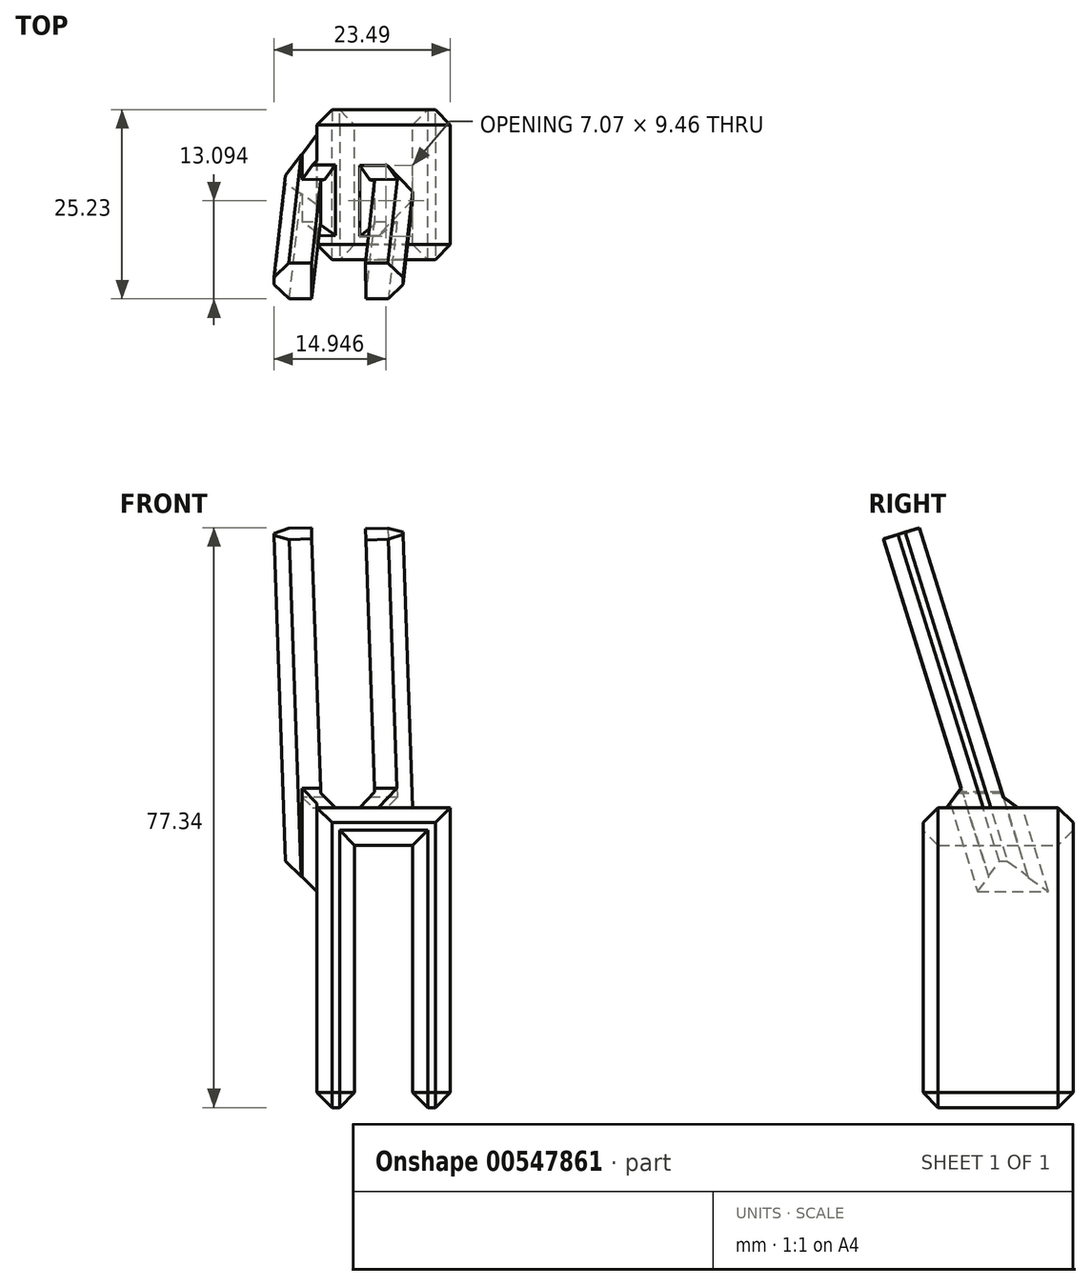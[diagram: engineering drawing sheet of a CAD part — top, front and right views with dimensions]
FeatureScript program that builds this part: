
annotation { "Feature Type Name" : "Feature", "Feature Type Description" : "" }
export const myFeature = defineFeature(function(context is Context, id is Id, definition is map)
    precondition{}
    {
        {
            var Q0;
            Q0=qCreatedBy(makeId("Front.planeOp"),FACE);
            var sketch = newSketch(context, id + "F0", { "sketchPlane" : qUnion([Q0])});
            skLineSegment(sketch, "E0", {"start": v(0, 17.78) * mm, "end": v(40, 17.78) * mm});
            skLineSegment(sketch, "E1", {"start": v(40, 17.78) * mm, "end": v(40, 0.03) * mm});
            skLineSegment(sketch, "E2", {"start": v(40, 0.03) * mm, "end": v(0, 0.03) * mm});
            skLineSegment(sketch, "E3", {"start": v(0, 0.03) * mm, "end": v(0, 5.03) * mm});
            skLineSegment(sketch, "E4", {"start": v(0, 5.03) * mm, "end": v(35, 5.03) * mm});
            skLineSegment(sketch, "E5", {"start": v(35, 5.03) * mm, "end": v(35, 12.78) * mm});
            skLineSegment(sketch, "E6", {"start": v(35, 12.78) * mm, "end": v(0, 12.78) * mm});
            skLineSegment(sketch, "E7", {"start": v(0, 12.78) * mm, "end": v(0, 17.78) * mm});
            skSolve(sketch);
        }
        {
            var Q0;
            Q0=makeQuery(id+"F0.imprint","IMPRINT",FACE,{"disambiguationData":[TD([[makeQuery(id+"F0.imprint","IMPRINT",EDGE,{"derivedFrom":sQuery(id+"F0.wireOp",EDGE,"E0")}),-1.0]])]});
            extrude(context, id + "F1", {"entities" : qUnion([Q0]), "endBound" : BoundingType.SYMMETRIC, "depth" : 20 * mm, "offsetDistance" : 25 * mm});
        }
        {
            var Q0;
            Q0=qCreatedBy(makeId("Top.planeOp"),FACE);
            var sketch = newSketch(context, id + "F2", { "sketchPlane" : qUnion([Q0])});
            skLineSegment(sketch, "E8", {"start": v(39, 1.42) * mm, "end": v(77.2, -10.46) * mm});
            skLineSegment(sketch, "E9", {"start": v(77.2, -10.46) * mm, "end": v(75.71, -15.23) * mm});
            skLineSegment(sketch, "E10", {"start": v(75.71, -15.23) * mm, "end": v(39, -3.82) * mm});
            skLineSegment(sketch, "E11", {"start": v(39, -3.82) * mm, "end": v(39, 1.42) * mm});
            skSolve(sketch);
        }
        {
            var Q0;
            Q0=makeQuery(id+"F2.imprint","IMPRINT",FACE,{"disambiguationData":[TD([[makeQuery(id+"F2.imprint","IMPRINT",EDGE,{"derivedFrom":sQuery(id+"F2.wireOp",EDGE,"E8")}),-1.0]])]});
            var Q1;
            Q1=sQuery(id+"F2.wireOp",EDGE,"E10");
            var Q2;
            Q2=sQuery(id+"F2.wireOp",EDGE,"E9");
            var Q3;
            Q3=sQuery(id+"F2.wireOp",EDGE,"E11");
            var Q4;
            Q4=sQuery(id+"F2.wireOp",EDGE,"E8");
            extrude(context, id + "F3", {"entities" : qUnion([Q0]), "surfaceEntities" : qUnion([Q1, Q2, Q3, Q4]), "depth" : 5 * mm, "offsetDistance" : 25 * mm});
        }
        {
            var Q0;
            Q0=makeQuery(id+"F3.opExtrude","SWEPT_BODY",BODY,{"disambiguationData":[OSD([sQuery(id+"F2.wireOp",EDGE,"E8"),sQuery(id+"F2.wireOp",EDGE,"E9"),sQuery(id+"F2.wireOp",EDGE,"E10"),sQuery(id+"F2.wireOp",EDGE,"E11")])]});
            var Q1;
            Q1=makeQuery(id+"F3.opExtrude","CAP_EDGE",EDGE,{"disambiguationData":[OSD([sQuery(id+"F2.wireOp",EDGE,"E11")])],"isStart":false});
            transform(context, id + "F4", {"entities" : qUnion([Q0]), "transformType" : TransformType.ROTATION, "transformAxis" : qUnion([Q1]), "angle" : 2 * degree, "oppositeDirection" : true, "makeCopy" : false});
        }
        {
            var Q0;
            Q0=makeQuery(id+"F3.opExtrude","SWEPT_BODY",BODY,{"disambiguationData":[OSD([sQuery(id+"F2.wireOp",EDGE,"E8"),sQuery(id+"F2.wireOp",EDGE,"E9"),sQuery(id+"F2.wireOp",EDGE,"E10"),sQuery(id+"F2.wireOp",EDGE,"E11")])]});
            var Q1;
            Q1=qCreatedBy(makeId("Top.planeOp"),FACE);
            transform(context, id + "F5", {"entities" : qUnion([Q0]), "transformType" : TransformType.TRANSLATION_DISTANCE, "transformDirection" : qUnion([Q1]), "distance" : 5 * mm, "makeCopy" : false});
        }
        {
            var Q0;
            Q0=makeQuery(id+"F3.opExtrude","SWEPT_BODY",BODY,{"disambiguationData":[OSD([sQuery(id+"F2.wireOp",EDGE,"E8"),sQuery(id+"F2.wireOp",EDGE,"E9"),sQuery(id+"F2.wireOp",EDGE,"E10"),sQuery(id+"F2.wireOp",EDGE,"E11")])]});
            transform(context, id + "F6", {"entities" : qUnion([Q0]), "transformType" : TransformType.COPY});
        }
        {
            var Q0;
            Q0=makeQuery(id+"F3.opExtrude","SWEPT_BODY",BODY,{"disambiguationData":[OSD([sQuery(id+"F2.wireOp",EDGE,"E8"),sQuery(id+"F2.wireOp",EDGE,"E9"),sQuery(id+"F2.wireOp",EDGE,"E10"),sQuery(id+"F2.wireOp",EDGE,"E11")])]});
            var Q1;
            Q1=qCreatedBy(makeId("Top.planeOp"),FACE);
            transform(context, id + "F7", {"entities" : qUnion([Q0]), "transformType" : TransformType.TRANSLATION_DISTANCE, "transformDirection" : qUnion([Q1]), "distance" : 12.2 * mm, "makeCopy" : false});
        }
        {
            var Q0;
            Q0=makeQuery(id+"F1.opExtrude","SWEPT_BODY",BODY,{"disambiguationData":[OSD([sQuery(id+"F0.wireOp",EDGE,"E0"),sQuery(id+"F0.wireOp",EDGE,"E1"),sQuery(id+"F0.wireOp",EDGE,"E2"),sQuery(id+"F0.wireOp",EDGE,"E3"),sQuery(id+"F0.wireOp",EDGE,"E4"),sQuery(id+"F0.wireOp",EDGE,"E5"),sQuery(id+"F0.wireOp",EDGE,"E6"),sQuery(id+"F0.wireOp",EDGE,"E7")])]});
            var Q1;
            Q1=makeQuery(id+"F3.opExtrude","SWEPT_BODY",BODY,{"disambiguationData":[OSD([sQuery(id+"F2.wireOp",EDGE,"E8"),sQuery(id+"F2.wireOp",EDGE,"E9"),sQuery(id+"F2.wireOp",EDGE,"E10"),sQuery(id+"F2.wireOp",EDGE,"E11")])]});
            var Q2;
            Q2=makeQuery(id+"F6.opPattern","COPY",BODY,{"derivedFrom":makeQuery(id+"F3.opExtrude","SWEPT_BODY",BODY,{"disambiguationData":[OSD([sQuery(id+"F2.wireOp",EDGE,"E8"),sQuery(id+"F2.wireOp",EDGE,"E9"),sQuery(id+"F2.wireOp",EDGE,"E10"),sQuery(id+"F2.wireOp",EDGE,"E11")])]}),"instanceName":"1"});
            booleanBodies(context, id + "F8", {"operationType" : BooleanOperationType.UNION, "tools" : qUnion([Q0, Q1, Q2])});
        }
        {
            var Q0;
            Q0=makeQuery(id+"F8.opBoolean","INTERSECT",EDGE,{"derivedFrom":[makeQuery(id+"F1.opExtrude","SWEPT_FACE",FACE,{"disambiguationData":[OSD([sQuery(id+"F0.wireOp",EDGE,"E0")])]}),makeQuery(id+"F3.opExtrude","SWEPT_FACE",FACE,{"disambiguationData":[OSD([sQuery(id+"F2.wireOp",EDGE,"E11")])]})]});
            chamfer(context, id + "F9", {"entities" : qUnion([Q0]), "width" : 10 * mm, "tangentPropagation" : true});
        }
        {
            var Q0;
            Q0=makeQuery(id+"F3.opExtrude","CAP_EDGE",EDGE,{"disambiguationData":[OSD([sQuery(id+"F2.wireOp",EDGE,"E10")])],"isStart":false});
            var Q1;
            Q1=makeQuery(id+"F3.opExtrude","CAP_EDGE",EDGE,{"disambiguationData":[OSD([sQuery(id+"F2.wireOp",EDGE,"E8")])],"isStart":false});
            var Q2;
            Q2=makeQuery(id+"F6.opPattern","COPY",EDGE,{"derivedFrom":makeQuery(id+"F3.opExtrude","CAP_EDGE",EDGE,{"disambiguationData":[OSD([sQuery(id+"F2.wireOp",EDGE,"E10")])],"isStart":true}),"instanceName":"1"});
            var Q3;
            Q3=makeQuery(id+"F6.opPattern","COPY",EDGE,{"derivedFrom":makeQuery(id+"F3.opExtrude","CAP_EDGE",EDGE,{"disambiguationData":[OSD([sQuery(id+"F2.wireOp",EDGE,"E8")])],"isStart":true}),"instanceName":"1"});
            var Q4;
            Q4=makeQuery(id+"F1.opExtrude","CAP_FACE",FACE,{"disambiguationData":[OSD([sQuery(id+"F0.wireOp",EDGE,"E0"),sQuery(id+"F0.wireOp",EDGE,"E1"),sQuery(id+"F0.wireOp",EDGE,"E2"),sQuery(id+"F0.wireOp",EDGE,"E3"),sQuery(id+"F0.wireOp",EDGE,"E4"),sQuery(id+"F0.wireOp",EDGE,"E5"),sQuery(id+"F0.wireOp",EDGE,"E6"),sQuery(id+"F0.wireOp",EDGE,"E7")])],"isStart":false});
            var Q5;
            Q5=makeQuery(id+"F1.opExtrude","CAP_FACE",FACE,{"disambiguationData":[OSD([sQuery(id+"F0.wireOp",EDGE,"E0"),sQuery(id+"F0.wireOp",EDGE,"E1"),sQuery(id+"F0.wireOp",EDGE,"E2"),sQuery(id+"F0.wireOp",EDGE,"E3"),sQuery(id+"F0.wireOp",EDGE,"E4"),sQuery(id+"F0.wireOp",EDGE,"E5"),sQuery(id+"F0.wireOp",EDGE,"E6"),sQuery(id+"F0.wireOp",EDGE,"E7")])],"isStart":true});
            var Q6;
            Q6=makeQuery(id+"F1.opExtrude","SWEPT_EDGE",EDGE,{"disambiguationData":[OSD([sQuery(id+"F0.wireOp",EDGE,"E0"),sQuery(id+"F0.wireOp",EDGE,"E7")])]});
            var Q7;
            Q7=makeQuery(id+"F1.opExtrude","SWEPT_EDGE",EDGE,{"disambiguationData":[OSD([sQuery(id+"F0.wireOp",EDGE,"E6"),sQuery(id+"F0.wireOp",EDGE,"E7")])]});
            var Q8;
            Q8=makeQuery(id+"F1.opExtrude","SWEPT_EDGE",EDGE,{"disambiguationData":[OSD([sQuery(id+"F0.wireOp",EDGE,"E3"),sQuery(id+"F0.wireOp",EDGE,"E4")])]});
            var Q9;
            Q9=makeQuery(id+"F1.opExtrude","SWEPT_EDGE",EDGE,{"disambiguationData":[OSD([sQuery(id+"F0.wireOp",EDGE,"E2"),sQuery(id+"F0.wireOp",EDGE,"E3")])]});
            chamfer(context, id + "F10", {"entities" : qUnion([Q0, Q1, Q2, Q3, Q4, Q5, Q6, Q7, Q8, Q9]), "width" : 2 * mm, "tangentPropagation" : true});
        }
        {
            var Q0;
            Q0=makeQuery(id+"F1.opExtrude","SWEPT_BODY",BODY,{"disambiguationData":[OSD([sQuery(id+"F0.wireOp",EDGE,"E0"),sQuery(id+"F0.wireOp",EDGE,"E1"),sQuery(id+"F0.wireOp",EDGE,"E2"),sQuery(id+"F0.wireOp",EDGE,"E3"),sQuery(id+"F0.wireOp",EDGE,"E4"),sQuery(id+"F0.wireOp",EDGE,"E5"),sQuery(id+"F0.wireOp",EDGE,"E6"),sQuery(id+"F0.wireOp",EDGE,"E7")])]});
            var Q1;
            {var subQ0=sQuery(id+"F0.wireOp",EDGE,"E2");Q1=makeQuery(id+"F10.opChamfer","BLEND_EDGE",EDGE,{"blendedFrom":[makeQuery(id+"F1.opExtrude","SWEPT_EDGE",EDGE,{"disambiguationData":[OSD([subQ0,sQuery(id+"F0.wireOp",EDGE,"E3")])]}),makeQuery(id+"F1.opExtrude","SWEPT_FACE",FACE,{"disambiguationData":[OSD([subQ0])]})],"blendedInto":[makeQuery(id+"F1.opExtrude","SWEPT_FACE",FACE,{"disambiguationData":[OSD([subQ0])]})]});}
            transform(context, id + "F11", {"entities" : qUnion([Q0]), "transformType" : TransformType.ROTATION, "transformAxis" : qUnion([Q1]), "angle" : 90 * degree, "oppositeDirection" : true, "makeCopy" : false});
        }
        {
            var Q0;
            Q0=makeQuery(id+"F8.opBoolean","INTERSECT",EDGE,{"derivedFrom":[makeQuery(id+"F1.opExtrude","SWEPT_FACE",FACE,{"disambiguationData":[OSD([sQuery(id+"F0.wireOp",EDGE,"E0")])]}),makeQuery(id+"F3.opExtrude","SWEPT_FACE",FACE,{"disambiguationData":[OSD([sQuery(id+"F2.wireOp",EDGE,"E10")])]})]});
            var Q1;
            Q1=makeQuery(id+"F8.opBoolean","INTERSECT",EDGE,{"derivedFrom":[makeQuery(id+"F1.opExtrude","SWEPT_FACE",FACE,{"disambiguationData":[OSD([sQuery(id+"F0.wireOp",EDGE,"E0")])]}),makeQuery(id+"F3.opExtrude","SWEPT_FACE",FACE,{"disambiguationData":[OSD([sQuery(id+"F2.wireOp",EDGE,"E8")])]})]});
            var Q2;
            Q2=makeQuery(id+"F8.opBoolean","INTERSECT",EDGE,{"derivedFrom":[makeQuery(id+"F1.opExtrude","SWEPT_FACE",FACE,{"disambiguationData":[OSD([sQuery(id+"F0.wireOp",EDGE,"E1")])]}),makeQuery(id+"F3.opExtrude","CAP_FACE",FACE,{"disambiguationData":[OSD([sQuery(id+"F2.wireOp",EDGE,"E8"),sQuery(id+"F2.wireOp",EDGE,"E9"),sQuery(id+"F2.wireOp",EDGE,"E10"),sQuery(id+"F2.wireOp",EDGE,"E11")])],"isStart":true})]});
            var Q3;
            Q3=makeQuery(id+"F8.opBoolean","INTERSECT",EDGE,{"derivedFrom":[makeQuery(id+"F1.opExtrude","SWEPT_FACE",FACE,{"disambiguationData":[OSD([sQuery(id+"F0.wireOp",EDGE,"E1")])]}),makeQuery(id+"F6.opPattern","COPY",FACE,{"derivedFrom":makeQuery(id+"F3.opExtrude","CAP_FACE",FACE,{"disambiguationData":[OSD([sQuery(id+"F2.wireOp",EDGE,"E8"),sQuery(id+"F2.wireOp",EDGE,"E9"),sQuery(id+"F2.wireOp",EDGE,"E10"),sQuery(id+"F2.wireOp",EDGE,"E11")])],"isStart":false}),"instanceName":"1"})]});
            chamfer(context, id + "F12", {"entities" : qUnion([Q0, Q1, Q2, Q3]), "width" : 2 * mm, "tangentPropagation" : true});
        }
        {
            var Q0;
            Q0=makeQuery(id+"F8.opBoolean","INTERSECT",EDGE,{"derivedFrom":[makeQuery(id+"F1.opExtrude","SWEPT_FACE",FACE,{"disambiguationData":[OSD([sQuery(id+"F0.wireOp",EDGE,"E1")])]}),makeQuery(id+"F3.opExtrude","SWEPT_FACE",FACE,{"disambiguationData":[OSD([sQuery(id+"F2.wireOp",EDGE,"E10")])]})]});
            var Q1;
            Q1=makeQuery(id+"F8.opBoolean","INTERSECT",EDGE,{"derivedFrom":[makeQuery(id+"F1.opExtrude","SWEPT_FACE",FACE,{"disambiguationData":[OSD([sQuery(id+"F0.wireOp",EDGE,"E1")])]}),makeQuery(id+"F3.opExtrude","SWEPT_FACE",FACE,{"disambiguationData":[OSD([sQuery(id+"F2.wireOp",EDGE,"E8")])]})]});
            var Q2;
            Q2=makeQuery(id+"F8.opBoolean","INTERSECT",EDGE,{"derivedFrom":[makeQuery(id+"F1.opExtrude","SWEPT_FACE",FACE,{"disambiguationData":[OSD([sQuery(id+"F0.wireOp",EDGE,"E1")])]}),makeQuery(id+"F6.opPattern","COPY",FACE,{"derivedFrom":makeQuery(id+"F3.opExtrude","SWEPT_FACE",FACE,{"disambiguationData":[OSD([sQuery(id+"F2.wireOp",EDGE,"E8")])]}),"instanceName":"1"})]});
            var Q3;
            Q3=makeQuery(id+"F8.opBoolean","INTERSECT",EDGE,{"derivedFrom":[makeQuery(id+"F1.opExtrude","SWEPT_FACE",FACE,{"disambiguationData":[OSD([sQuery(id+"F0.wireOp",EDGE,"E1")])]}),makeQuery(id+"F6.opPattern","COPY",FACE,{"derivedFrom":makeQuery(id+"F3.opExtrude","SWEPT_FACE",FACE,{"disambiguationData":[OSD([sQuery(id+"F2.wireOp",EDGE,"E10")])]}),"instanceName":"1"})]});
            chamfer(context, id + "F13", {"entities" : qUnion([Q0, Q1, Q2, Q3]), "width" : 2 * mm, "tangentPropagation" : true});
        }
    });
